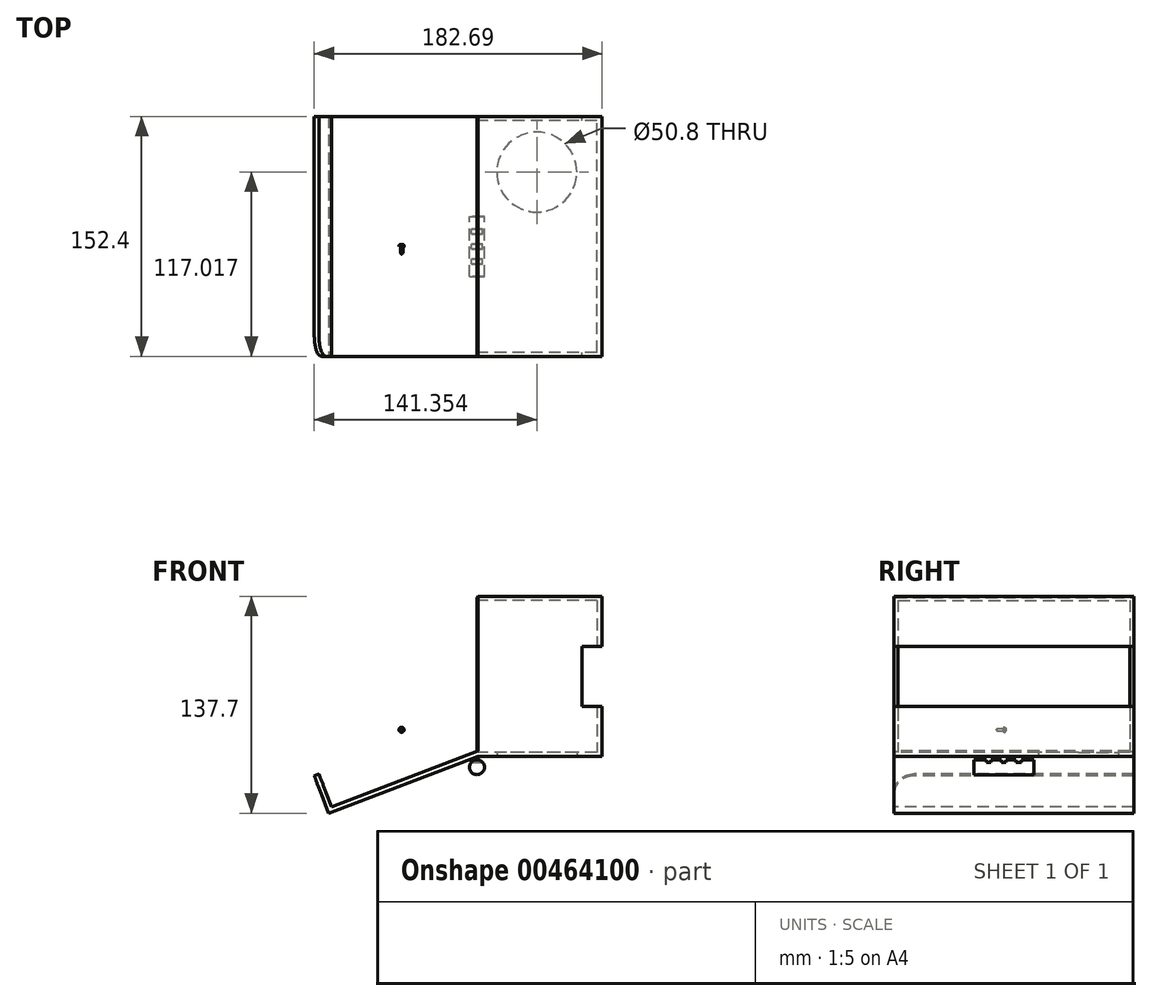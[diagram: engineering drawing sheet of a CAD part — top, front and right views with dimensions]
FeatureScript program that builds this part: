
annotation { "Feature Type Name" : "Feature", "Feature Type Description" : "" }
export const myFeature = defineFeature(function(context is Context, id is Id, definition is map)
    precondition{}
    {
        {
            var Q0;
            Q0=qCreatedBy(makeId("Front.planeOp"),FACE);
            var sketch = newSketch(context, id + "F0", { "sketchPlane" : qUnion([Q0])});
            skCircle(sketch, "E0", {"center": v(0, 0) * mm, "radius": 4.76 * mm});
            skSolve(sketch);
        }
        {
            var Q0;
            Q0=qSketchRegion(id+"F0",true);
            extrude(context, id + "F1", {"entities" : qUnion([Q0]), "endBound" : BoundingType.SYMMETRIC, "depth" : 38.1 * mm});
        }
        {
            var Q0;
            Q0=qCreatedBy(makeId("Right.planeOp"),FACE);
            var sketch = newSketch(context, id + "F2", { "sketchPlane" : qUnion([Q0])});
            skLineSegment(sketch, "E1.bottom", {"start": v(-1.59, 6.48) * mm, "end": v(1.59, 6.48) * mm});
            skLineSegment(sketch, "E1.top", {"start": v(-1.59, 3.18) * mm, "end": v(1.59, 3.18) * mm});
            skLineSegment(sketch, "E1.left", {"start": v(-1.59, 6.48) * mm, "end": v(-1.59, 3.18) * mm});
            skLineSegment(sketch, "E1.right", {"start": v(1.59, 6.48) * mm, "end": v(1.59, 3.18) * mm});
            skLineSegment(sketch, "E2.bottom", {"start": v(7.94, 6.48) * mm, "end": v(11.11, 6.48) * mm});
            skLineSegment(sketch, "E2.top", {"start": v(7.94, 3.17) * mm, "end": v(11.11, 3.18) * mm});
            skLineSegment(sketch, "E2.left", {"start": v(7.94, 6.48) * mm, "end": v(7.94, 3.17) * mm});
            skLineSegment(sketch, "E2.right", {"start": v(11.11, 6.48) * mm, "end": v(11.11, 3.18) * mm});
            skLineSegment(sketch, "E3.MirrorCS", {"start": v(-7.94, 6.48) * mm, "end": v(-11.11, 6.48) * mm});
            skLineSegment(sketch, "E4.MirrorCS", {"start": v(-11.11, 6.48) * mm, "end": v(-11.11, 3.18) * mm});
            skLineSegment(sketch, "E5.MirrorCS", {"start": v(-7.94, 3.17) * mm, "end": v(-11.11, 3.18) * mm});
            skLineSegment(sketch, "E6.MirrorCS", {"start": v(-7.94, 6.48) * mm, "end": v(-7.94, 3.17) * mm});
            skSolve(sketch);
        }
        {
            var Q0;
            Q0=qSketchRegion(id+"F2",true);
            extrude(context, id + "F3", {"entities" : qUnion([Q0]), "operationType" : NewBodyOperationType.REMOVE, "endBound" : BoundingType.SYMMETRIC, "oppositeDirection" : true, "depth" : 25.4 * mm});
        }
        {
            var Q0;
            Q0=qCreatedBy(makeId("Right.planeOp"),FACE);
            var sketch = newSketch(context, id + "F4", { "sketchPlane" : qUnion([Q0])});
            skLineSegment(sketch, "E7.bottom", {"start": v(-69.66, 108.51) * mm, "end": v(82.74, 108.51) * mm});
            skLineSegment(sketch, "E7.top", {"start": v(-69.66, 6.91) * mm, "end": v(82.74, 6.91) * mm});
            skLineSegment(sketch, "E7.left", {"start": v(-69.66, 108.51) * mm, "end": v(-69.66, 6.91) * mm});
            skLineSegment(sketch, "E7.right", {"start": v(82.74, 108.51) * mm, "end": v(82.74, 6.91) * mm});
            skSolve(sketch);
        }
        {
            var Q0;
            Q0=qSketchRegion(id+"F4",true);
            extrude(context, id + "F5", {"entities" : qUnion([Q0]), "depth" : 76.2 * mm});
        }
        {
            var Q0;
            Q0=makeQuery(id+"F5.opExtrude","CAP_FACE",FACE,{"disambiguationData":[OSD([sQuery(id+"F4.wireOp",EDGE,"E7.bottom"),sQuery(id+"F4.wireOp",EDGE,"E7.top"),sQuery(id+"F4.wireOp",EDGE,"E7.left"),sQuery(id+"F4.wireOp",EDGE,"E7.right")])],"isStart":false});
            shell(context, id + "F6", {"entities" : qUnion([Q0]), "thickness" : 2.54 * mm});
        }
        {
            var Q0;
            Q0=makeQuery(id+"F5.opExtrude","CAP_FACE",FACE,{"disambiguationData":[OSD([sQuery(id+"F4.wireOp",EDGE,"E7.bottom"),sQuery(id+"F4.wireOp",EDGE,"E7.top"),sQuery(id+"F4.wireOp",EDGE,"E7.left"),sQuery(id+"F4.wireOp",EDGE,"E7.right")])],"isStart":false});
            var sketch = newSketch(context, id + "F7", { "sketchPlane" : qUnion([Q0])});
            skLineSegment(sketch, "E8.bottom", {"start": v(-69.66, 108.51) * mm, "end": v(82.74, 108.51) * mm});
            skLineSegment(sketch, "E8.top", {"start": v(-69.66, 6.91) * mm, "end": v(82.74, 6.91) * mm});
            skLineSegment(sketch, "E8.left", {"start": v(-69.66, 108.51) * mm, "end": v(-69.66, 6.91) * mm});
            skLineSegment(sketch, "E8.right", {"start": v(82.74, 108.51) * mm, "end": v(82.74, 6.91) * mm});
            skSolve(sketch);
        }
        {
            var Q0;
            Q0=qSketchRegion(id+"F7",true);
            extrude(context, id + "F8", {"entities" : qUnion([Q0]), "operationType" : NewBodyOperationType.ADD, "depth" : 3.17 * mm});
        }
        {
            var Q0;
            Q0=makeQuery(id+"F8.opExtrude","CAP_FACE",FACE,{"disambiguationData":[OSD([sQuery(id+"F7.wireOp",EDGE,"E8.bottom"),sQuery(id+"F7.wireOp",EDGE,"E8.top"),sQuery(id+"F7.wireOp",EDGE,"E8.left"),sQuery(id+"F7.wireOp",EDGE,"E8.right")])],"isStart":false});
            var sketch = newSketch(context, id + "F9", { "sketchPlane" : qUnion([Q0])});
            skLineSegment(sketch, "E9.bottom", {"start": v(-82.06, 76.76) * mm, "end": v(95.74, 76.76) * mm});
            skLineSegment(sketch, "E9.top", {"start": v(-82.06, 38.66) * mm, "end": v(95.74, 38.66) * mm});
            skLineSegment(sketch, "E9.left", {"start": v(-82.06, 76.76) * mm, "end": v(-82.06, 38.66) * mm});
            skLineSegment(sketch, "E9.right", {"start": v(95.74, 76.76) * mm, "end": v(95.74, 38.66) * mm});
            skLineSegment(sketch, "E10", {"start": v(-69.66, 57.71) * mm, "end": v(82.74, 57.71) * mm, "construction": true});
            skSolve(sketch);
        }
        {
            var Q0;
            Q0=qSketchRegion(id+"F9",true);
            extrude(context, id + "F10", {"entities" : qUnion([Q0]), "operationType" : NewBodyOperationType.REMOVE, "oppositeDirection" : true, "depth" : 12.7 * mm});
        }
        {
            var Q0;
            Q0=makeQuery(id+"F8.boolean.opBoolean","MERGE",FACE,{"derivedFrom":[makeQuery(id+"F5.opExtrude","SWEPT_FACE",FACE,{"disambiguationData":[OSD([sQuery(id+"F4.wireOp",EDGE,"E7.top")])]}),makeQuery(id+"F8.opExtrude","SWEPT_FACE",FACE,{"disambiguationData":[OSD([sQuery(id+"F7.wireOp",EDGE,"E8.top")])]})]});
            var sketch = newSketch(context, id + "F11", { "sketchPlane" : qUnion([Q0])});
            skCircle(sketch, "E11", {"center": v(38.04, -47.36) * mm, "radius": 25.4 * mm});
            skSolve(sketch);
        }
        {
            var Q0;
            Q0=qSketchRegion(id+"F11",true);
            extrude(context, id + "F12", {"entities" : qUnion([Q0]), "operationType" : NewBodyOperationType.REMOVE, "oppositeDirection" : true, "depth" : 25.4 * mm});
        }
        {
            var Q0;
            Q0=qCreatedBy(makeId("Front.planeOp"),FACE);
            var sketch = newSketch(context, id + "F13", { "sketchPlane" : qUnion([Q0])});
            skCircle(sketch, "E12", {"center": v(-47.88, 23.8) * mm, "radius": 0.8 * mm});
            skSolve(sketch);
        }
        {
            var Q0;
            Q0=qSketchRegion(id+"F13",true);
            extrude(context, id + "F14", {"entities" : qUnion([Q0]), "depth" : 4.76 * mm});
        }
        {
            var Q0;
            Q0=makeQuery(id+"F14.opExtrude","CAP_EDGE",EDGE,{"disambiguationData":[OSD([sQuery(id+"F13.wireOp",EDGE,"E12")])],"isStart":false});
            var Q1;
            Q1=makeQuery(id+"F5.opExtrude","CAP_FACE",FACE,{"disambiguationData":[OSD([sQuery(id+"F4.wireOp",EDGE,"E7.bottom"),sQuery(id+"F4.wireOp",EDGE,"E7.top"),sQuery(id+"F4.wireOp",EDGE,"E7.left"),sQuery(id+"F4.wireOp",EDGE,"E7.right")])],"isStart":true});
            chamfer(context, id + "F15", {"entities" : qUnion([Q0, Q1]), "width" : 0.69 * mm, "tangentPropagation" : true});
        }
        {
            var Q0;
            Q0=makeQuery(id+"F14.opExtrude","CAP_FACE",FACE,{"disambiguationData":[OSD([sQuery(id+"F13.wireOp",EDGE,"E12")])],"isStart":true});
            var sketch = newSketch(context, id + "F16", { "sketchPlane" : qUnion([Q0])});
            skCircle(sketch, "E13", {"center": v(47.88, 23.8) * mm, "radius": 1.59 * mm});
            skSolve(sketch);
        }
        {
            var Q0;
            Q0=qSketchRegion(id+"F16",true);
            extrude(context, id + "F17", {"entities" : qUnion([Q0]), "operationType" : NewBodyOperationType.ADD, "depth" : 1.27 * mm});
        }
        {
            var Q0;
            Q0=makeQuery(id+"F17.opExtrude","CAP_EDGE",EDGE,{"disambiguationData":[OSD([sQuery(id+"F16.wireOp",EDGE,"E13")])],"isStart":false});
            fillet(context, id + "F18", {"entities" : qUnion([Q0]), "radius" : 0.76 * mm, "tangentPropagation" : true, "allowEdgeOverflow" : false});
        }
        {
            var Q0;
            Q0=makeQuery(id+"F17.opExtrude","CAP_FACE",FACE,{"disambiguationData":[OSD([sQuery(id+"F16.wireOp",EDGE,"E13")])],"isStart":false});
            var sketch = newSketch(context, id + "F19", { "sketchPlane" : qUnion([Q0])});
            skLineSegment(sketch, "E14.bottom", {"start": v(47.76, 24.36) * mm, "end": v(47.98, 24.36) * mm});
            skLineSegment(sketch, "E14.top", {"start": v(47.76, 23.19) * mm, "end": v(47.98, 23.19) * mm});
            skLineSegment(sketch, "E14.left", {"start": v(47.76, 24.36) * mm, "end": v(47.76, 23.19) * mm});
            skLineSegment(sketch, "E14.right", {"start": v(47.98, 24.36) * mm, "end": v(47.98, 23.19) * mm});
            skSolve(sketch);
        }
        {
            var Q0;
            Q0=qSketchRegion(id+"F19",true);
            extrude(context, id + "F20", {"entities" : qUnion([Q0]), "operationType" : NewBodyOperationType.REMOVE, "oppositeDirection" : true, "depth" : 0.76 * mm});
        }
        {
            var Q0;
            {var subQ0=sQuery(id+"F16.wireOp",EDGE,"E13");Q0=makeQuery(id+"F20.boolean.opBoolean","SPLIT",FACE,{"disambiguationData":[TD([makeQuery(id+"F20.opExtrude","SWEPT_FACE",FACE,{"disambiguationData":[OSD([sQuery(id+"F19.wireOp",EDGE,"E14.right")])]})])],"derivedFrom":makeQuery(id+"F17.opExtrude","CAP_FACE",FACE,{"disambiguationData":[OSD([subQ0])],"isStart":false})});}
            var sketch = newSketch(context, id + "F21", { "sketchPlane" : qUnion([Q0])});
            skLineSegment(sketch, "E15.bottom", {"start": v(47.45, 23.88) * mm, "end": v(48.3, 23.88) * mm});
            skLineSegment(sketch, "E15.top", {"start": v(47.45, 23.67) * mm, "end": v(48.3, 23.67) * mm});
            skLineSegment(sketch, "E15.left", {"start": v(47.45, 23.88) * mm, "end": v(47.45, 23.67) * mm});
            skLineSegment(sketch, "E15.right", {"start": v(48.3, 23.88) * mm, "end": v(48.3, 23.67) * mm});
            skSolve(sketch);
        }
        {
            var Q0;
            Q0=qSketchRegion(id+"F21",true);
            extrude(context, id + "F22", {"entities" : qUnion([Q0]), "operationType" : NewBodyOperationType.REMOVE, "oppositeDirection" : true, "depth" : 0.76 * mm});
        }
        {
            var Q0;
            {var subQ0=sQuery(id+"F9.wireOp",EDGE,"E9.bottom");var subQ1=sQuery(id+"F4.wireOp",EDGE,"E7.left");var subQ2=sQuery(id+"F9.wireOp",EDGE,"E9.top");Q0=makeQuery(id+"F10.boolean.opBoolean","COPY",FACE,{"disambiguationData":[TD([makeQuery(id+"F5.opExtrude","SWEPT_FACE",FACE,{"disambiguationData":[OSD([subQ1])]})])],"derivedFrom":makeQuery(id+"F10.opExtrude","CAP_FACE",FACE,{"disambiguationData":[OSD([subQ0,subQ2,sQuery(id+"F9.wireOp",EDGE,"E9.left"),sQuery(id+"F9.wireOp",EDGE,"E9.right")])],"isStart":false})});}
            var sketch = newSketch(context, id + "F23", { "sketchPlane" : qUnion([Q0])});
            skLineSegment(sketch, "E16.bottom", {"start": v(-67.12, 76.76) * mm, "end": v(-86.17, 76.76) * mm});
            skLineSegment(sketch, "E16.top", {"start": v(-67.12, 38.66) * mm, "end": v(-86.17, 38.66) * mm});
            skLineSegment(sketch, "E16.left", {"start": v(-67.12, 76.76) * mm, "end": v(-67.12, 38.66) * mm});
            skLineSegment(sketch, "E16.right", {"start": v(-86.17, 76.76) * mm, "end": v(-86.17, 38.66) * mm});
            skLineSegment(sketch, "E17.bottom", {"start": v(80.2, 76.76) * mm, "end": v(99.25, 76.76) * mm});
            skLineSegment(sketch, "E17.top", {"start": v(80.2, 38.66) * mm, "end": v(99.25, 38.66) * mm});
            skLineSegment(sketch, "E17.left", {"start": v(80.2, 76.76) * mm, "end": v(80.2, 38.66) * mm});
            skLineSegment(sketch, "E17.right", {"start": v(99.25, 76.76) * mm, "end": v(99.25, 38.66) * mm});
            skSolve(sketch);
        }
        {
            var Q0;
            Q0=makeQuery(id+"F5.opExtrude","CAP_FACE",FACE,{"disambiguationData":[OSD([sQuery(id+"F4.wireOp",EDGE,"E7.bottom"),sQuery(id+"F4.wireOp",EDGE,"E7.top"),sQuery(id+"F4.wireOp",EDGE,"E7.left"),sQuery(id+"F4.wireOp",EDGE,"E7.right")])],"isStart":true});
            var sketch = newSketch(context, id + "F24", { "sketchPlane" : qUnion([Q0])});
            skLineSegment(sketch, "E18.bottom", {"start": v(67.12, 105.97) * mm, "end": v(-80.2, 105.97) * mm});
            skLineSegment(sketch, "E18.top", {"start": v(67.12, 9.45) * mm, "end": v(-80.2, 9.45) * mm});
            skLineSegment(sketch, "E18.left", {"start": v(67.12, 105.97) * mm, "end": v(67.12, 9.45) * mm});
            skLineSegment(sketch, "E18.right", {"start": v(-80.2, 105.97) * mm, "end": v(-80.2, 9.45) * mm});
            skPoint(sketch, "E18.middle", {"position": v(-6.54, 57.71) * mm});
            skSolve(sketch);
        }
        {
            var Q0;
            Q0 = qSketchRegion(id + "F24", true);
            extrude(context, id + "F25", {"entities" : qUnion([Q0]), "operationType" : NewBodyOperationType.REMOVE, "oppositeDirection" : true, "depth" : 25.4 * mm});
        }
        {
            var Q0;
            Q0=makeQuery(id+"F8.boolean.opBoolean","MERGE",FACE,{"derivedFrom":[makeQuery(id+"F5.opExtrude","SWEPT_FACE",FACE,{"disambiguationData":[OSD([sQuery(id+"F4.wireOp",EDGE,"E7.left")])]}),makeQuery(id+"F8.opExtrude","SWEPT_FACE",FACE,{"disambiguationData":[OSD([sQuery(id+"F7.wireOp",EDGE,"E8.left")])]})]});
            var sketch = newSketch(context, id + "F26", { "sketchPlane" : qUnion([Q0])});
            skLineSegment(sketch, "E19", {"start": v(0.69, 6.91) * mm, "end": v(-94.28, -29.19) * mm});
            skLineSegment(sketch, "E20", {"start": v(-94.28, -29.19) * mm, "end": v(-103.3, -5.44) * mm});
            skLineSegment(sketch, "E21", {"start": v(-103.3, -5.44) * mm, "end": v(-100.34, -4.32) * mm});
            skLineSegment(sketch, "E22", {"start": v(-100.34, -4.32) * mm, "end": v(-92.44, -25.1) * mm});
            skLineSegment(sketch, "E23", {"start": v(-92.44, -25.1) * mm, "end": v(0.69, 10.31) * mm});
            skLineSegment(sketch, "E24", {"start": v(0.69, 10.31) * mm, "end": v(0.69, 6.91) * mm});
            skSolve(sketch);
        }
        {
            var Q0;
            Q0=makeQuery(id+"F26.imprint","IMPRINT",FACE,{"disambiguationData":[TD([[makeQuery(id+"F26.imprint","IMPRINT",EDGE,{"derivedFrom":sQuery(id+"F26.wireOp",EDGE,"E19")}),-1.0]])]});
            var Q1;
            Q1=makeQuery(id+"F8.boolean.opBoolean","MERGE",FACE,{"derivedFrom":[makeQuery(id+"F5.opExtrude","SWEPT_FACE",FACE,{"disambiguationData":[OSD([sQuery(id+"F4.wireOp",EDGE,"E7.right")])]}),makeQuery(id+"F8.opExtrude","SWEPT_FACE",FACE,{"disambiguationData":[OSD([sQuery(id+"F7.wireOp",EDGE,"E8.right")])]})]});
            extrude(context, id + "F27", {"entities" : qUnion([Q0]), "operationType" : NewBodyOperationType.ADD, "endBound" : BoundingType.UP_TO_SURFACE, "oppositeDirection" : true, "endBoundEntityFace" : qUnion([Q1]), "depth" : 25.4 * mm});
        }
        {
            var Q0;
            Q0=makeQuery(id+"F27.opExtrude","TWEAK_EDGE",EDGE,{"derivedFrom":[makeQuery(id+"F8.boolean.opBoolean","MERGE",FACE,{"derivedFrom":[makeQuery(id+"F5.opExtrude","SWEPT_FACE",FACE,{"disambiguationData":[OSD([sQuery(id+"F4.wireOp",EDGE,"E7.right")])]}),makeQuery(id+"F8.opExtrude","SWEPT_FACE",FACE,{"disambiguationData":[OSD([sQuery(id+"F7.wireOp",EDGE,"E8.right")])]})]}),makeQuery(id+"F26.imprint","IMPRINT",EDGE,{"derivedFrom":sQuery(id+"F26.wireOp",EDGE,"E21")})]});
            var Q1;
            Q1=makeQuery(id+"F27.opExtrude","CAP_EDGE",EDGE,{"disambiguationData":[OSD([sQuery(id+"F26.wireOp",EDGE,"E21")])],"isStart":true});
            fillet(context, id + "F28", {"entities" : qUnion([Q0, Q1]), "radius" : 12.7 * mm, "tangentPropagation" : true, "allowEdgeOverflow" : false});
        }
    });
